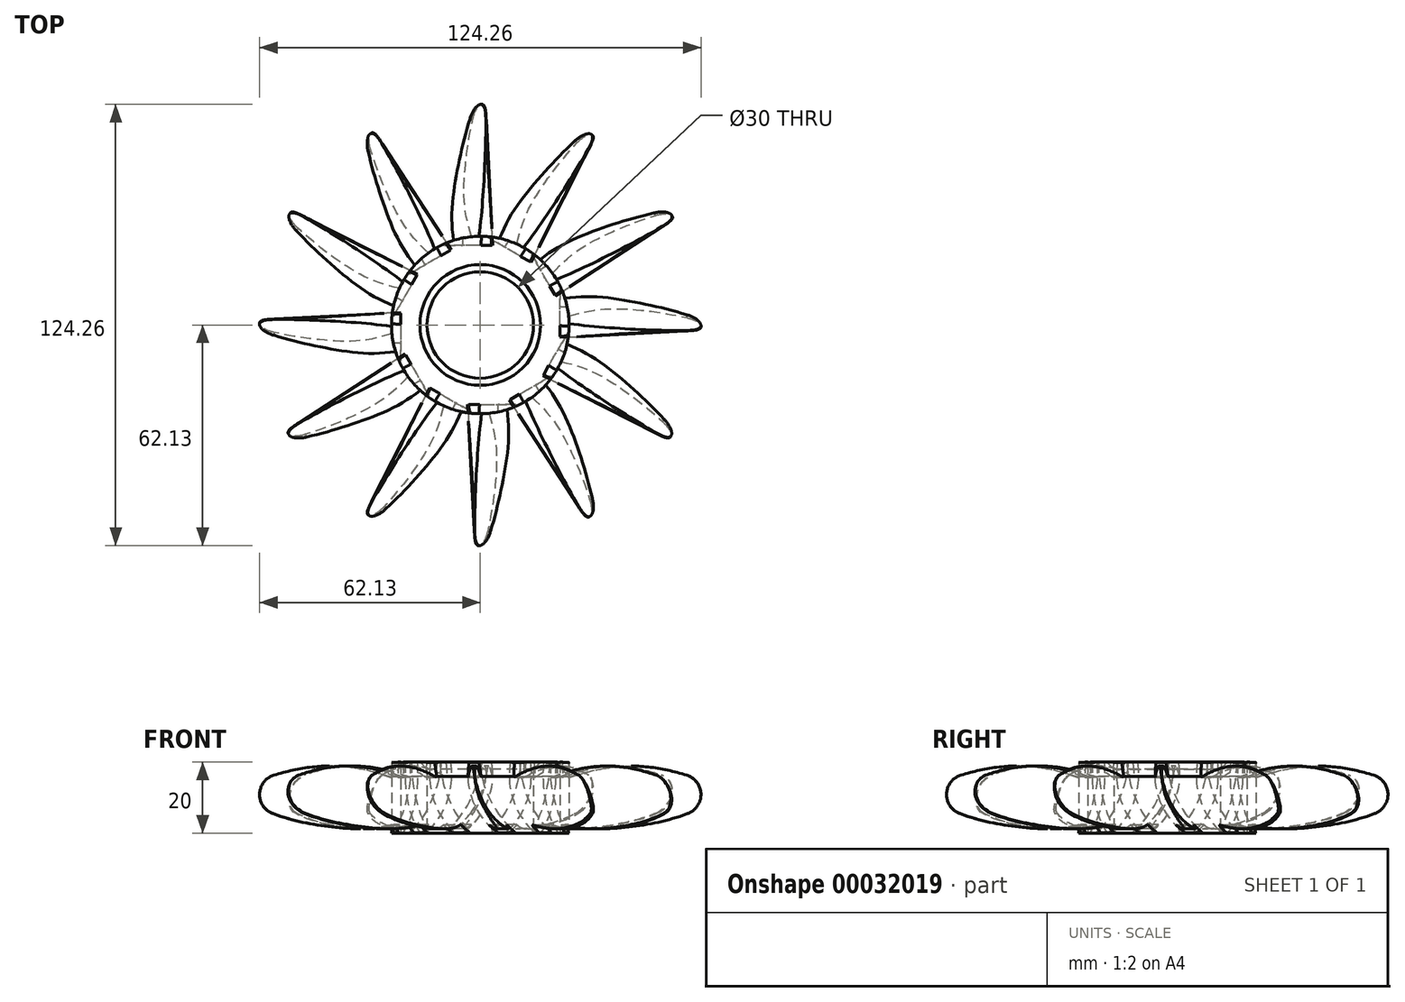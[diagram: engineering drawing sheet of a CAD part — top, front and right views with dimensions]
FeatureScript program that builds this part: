
annotation { "Feature Type Name" : "Feature", "Feature Type Description" : "" }
export const myFeature = defineFeature(function(context is Context, id is Id, definition is map)
    precondition{}
    {
        {
            var Q0;
            Q0=qCreatedBy(makeId("Top.planeOp"),FACE);
            var sketch = newSketch(context, id + "F0", { "sketchPlane" : qUnion([Q0])});
            skCircle(sketch, "E0", {"center": v(0, 0) * mm, "radius": 25 * mm});
            skCircle(sketch, "E1", {"center": v(0, 0) * mm, "radius": 15 * mm});
            skSolve(sketch);
        }
        {
            var Q0;
            Q0=makeQuery(id+"F0.imprint","IMPRINT",FACE,{"disambiguationData":[TD([[makeQuery(id+"F0.imprint","IMPRINT",EDGE,{"derivedFrom":sQuery(id+"F0.wireOp",EDGE,"E0")}),1.0]])]});
            extrude(context, id + "F1", {"entities" : qUnion([Q0]), "endBound" : BoundingType.SYMMETRIC, "depth" : 20 * mm});
        }
        {
            var Q0;
            Q0=qCreatedBy(makeId("Front.planeOp"),FACE);
            var sketch = newSketch(context, id + "F2", { "sketchPlane" : qUnion([Q0])});
            skLineSegment(sketch, "E2.0", {"start": v(-25, 10) * mm, "end": v(25, 10) * mm});
            skLineSegment(sketch, "E3.1", {"start": v(-25, -10) * mm, "end": v(25, -10) * mm});
            skArc(sketch, "E4", {"start": v(-0.2, 10) * mm, "mid": v(2.97, -1) * mm, "end": v(10.02, -10) * mm});
            skArc(sketch, "E5", {"start": v(-3.2, 10) * mm, "mid": v(-2.03, -1.2) * mm, "end": v(5.02, -10) * mm});
            skLineSegment(sketch, "E6", {"start": v(0, 0) * mm, "end": v(-2.48, 0) * mm, "construction": true});
            skLineSegment(sketch, "E7", {"start": v(0, 0) * mm, "end": v(2.48, 0) * mm, "construction": true});
            skSolve(sketch);
        }
        {
            var Q0;
            {var subQ1=sQuery(id+"F2.wireOp",EDGE,"E4");Q0=makeQuery(id+"F2.imprint","IMPRINT",FACE,{"disambiguationData":[TD([[makeQuery(id+"F2.imprint","IMPRINT",EDGE,{"derivedFrom":subQ1}),-1.0]])]});}
            extrude(context, id + "F3", {"entities" : qUnion([Q0]), "depth" : 40 * mm, "hasDraft" : true, "draftAngle" : 3 * degree, "draftPullDirection" : true});
        }
        {
            var Q0;
            Q0=makeQuery(id+"F3.opExtrude","SWEPT_BODY",BODY,{"disambiguationData":[OSD([sQuery(id+"F2.wireOp",EDGE,"E2.0"),sQuery(id+"F2.wireOp",EDGE,"E3.1"),sQuery(id+"F2.wireOp",EDGE,"E4"),sQuery(id+"F2.wireOp",EDGE,"E5")])]});
            transform(context, id + "F4", {"entities" : qUnion([Q0]), "transformType" : TransformType.TRANSLATION_3D, "dx" : 0 * mm, "dy" : -22.43 * mm, "dz" : 0 * mm, "makeCopy" : false});
        }
        {
            var Q0;
            Q0=makeQuery(id+"F3.opExtrude","SWEPT_BODY",BODY,{"disambiguationData":[OSD([sQuery(id+"F2.wireOp",EDGE,"E2.0"),sQuery(id+"F2.wireOp",EDGE,"E3.1"),sQuery(id+"F2.wireOp",EDGE,"E4"),sQuery(id+"F2.wireOp",EDGE,"E5")])]});
            var Q1;
            Q1=makeQuery(id+"F1.opExtrude","CAP_EDGE",EDGE,{"disambiguationData":[OSD([sQuery(id+"F0.wireOp",EDGE,"E0")])],"isStart":false});
            circularPattern(context, id + "F5", {"entities" : qUnion([Q0]), "axis" : qUnion([Q1]), "angle" : 360 * degree, "instanceCount" : 12, "equalSpace" : true});
        }
        {
            var Q0;
            Q0=qCreatedBy(makeId("Front.planeOp"),FACE);
            var sketch = newSketch(context, id + "F6", { "sketchPlane" : qUnion([Q0])});
            skLineSegment(sketch, "E8.0", {"start": v(-25, 10) * mm, "end": v(25, 10) * mm});
            skLineSegment(sketch, "E9.1", {"start": v(-25, -10) * mm, "end": v(25, -10) * mm});
            skLineSegment(sketch, "E10.2", {"start": v(62.7, 8.27) * mm, "end": v(62.69, -8.27) * mm});
            skLineSegment(sketch, "E11", {"start": v(25, 10) * mm, "end": v(25, -10) * mm});
            skFitSpline(sketch, "E12", {"points": [v(25, 5.66) * mm, v(43.48, 8.86) * mm, v(62.7, 4.75) * mm], "startDerivative": vector(37.13, 12.47) * mm, "endDerivative": vector(37.73, -14.16) * mm});
            skFitSpline(sketch, "E13", {"points": [v(25, -7.66) * mm, v(42.2, -8.27) * mm, v(62.7, -2.51) * mm], "startDerivative": vector(39.3, -9.22) * mm, "endDerivative": vector(35.55, 19.42) * mm});
            skLineSegment(sketch, "E14", {"start": v(58.15, 6.3) * mm, "end": v(58.15, -4.6) * mm});
            skArc(sketch, "E15", {"start": v(58.15, -4.6) * mm, "mid": v(62.14, 0.85) * mm, "end": v(58.15, 6.3) * mm});
            skLineSegment(sketch, "E16", {"start": v(25, 10) * mm, "end": v(62.7, 8.27) * mm});
            skLineSegment(sketch, "E17", {"start": v(25, -10) * mm, "end": v(62.69, -8.27) * mm});
            skSolve(sketch);
        }
        {
            var Q0;
            {var subQ0=sQuery(id+"F6.wireOp",EDGE,"E16");Q0=makeQuery(id+"F6.imprint","IMPRINT",FACE,{"disambiguationData":[TD([[makeQuery(id+"F6.imprint","IMPRINT",EDGE,{"derivedFrom":subQ0}),-1.0]])]});}
            var Q1;
            {var subQ0=sQuery(id+"F6.wireOp",EDGE,"E17");Q1=makeQuery(id+"F6.imprint","IMPRINT",FACE,{"disambiguationData":[TD([[makeQuery(id+"F6.imprint","IMPRINT",EDGE,{"derivedFrom":subQ0}),1.0]])]});}
            var Q2;
            {var subQ3=sQuery(id+"F6.wireOp",EDGE,"E12");var subQ5=sQuery(id+"F6.wireOp",EDGE,"E10.2");var subQ7=makeQuery(id+"F6.imprint","INTERSECT",VERTEX,{"derivedFrom":[subQ5,subQ3]});Q2=makeQuery(id+"F6.imprint","IMPRINT",FACE,{"disambiguationData":[TD([[makeQuery(id+"F6.imprint","IMPRINT",EDGE,{"disambiguationData":[TD([[subQ7,-1.0]])],"derivedFrom":subQ5}),-1.0]])]});}
            var Q3;
            Q3=makeQuery(id+"F1.opExtrude","CAP_EDGE",EDGE,{"disambiguationData":[OSD([sQuery(id+"F0.wireOp",EDGE,"E1")])],"isStart":false});
            revolve(context, id + "F7", {"operationType" : NewBodyOperationType.REMOVE, "entities" : qUnion([Q0, Q1, Q2]), "axis" : qUnion([Q3]), "revolveType" : RevolveType.FULL, "oppositeDirection" : true});
        }
        {
            var Q0;
            Q0=makeQuery(id+"F1.opExtrude","CAP_EDGE",EDGE,{"disambiguationData":[OSD([sQuery(id+"F0.wireOp",EDGE,"E0")])],"isStart":false});
            chamfer(context, id + "F8", {"entities" : qUnion([Q0]), "width" : 4 * mm, "tangentPropagation" : true});
        }
        {
            var Q0;
            {var subQ0=sQuery(id+"F0.wireOp",EDGE,"E0");Q0=makeQuery(id+"F8.opChamfer","BLEND_EDGE",EDGE,{"blendedFrom":[makeQuery(id+"F1.opExtrude","CAP_EDGE",EDGE,{"disambiguationData":[OSD([subQ0])],"isStart":false}),makeQuery(id+"F1.opExtrude","CAP_FACE",FACE,{"disambiguationData":[OSD([subQ0,sQuery(id+"F0.wireOp",EDGE,"E1")])],"isStart":false})],"blendedInto":[makeQuery(id+"F1.opExtrude","CAP_FACE",FACE,{"disambiguationData":[OSD([subQ0,sQuery(id+"F0.wireOp",EDGE,"E1")])],"isStart":false})]});}
            fillet(context, id + "F9", {"entities" : qUnion([Q0]), "radius" : 1 * mm, "tangentPropagation" : true, "allowEdgeOverflow" : false});
        }
        {
            var Q0;
            Q0=makeQuery(id+"F1.opExtrude","CAP_EDGE",EDGE,{"disambiguationData":[OSD([sQuery(id+"F0.wireOp",EDGE,"E1")])],"isStart":false});
            chamfer(context, id + "F10", {"entities" : qUnion([Q0]), "width" : 2 * mm, "tangentPropagation" : true});
        }
    });
